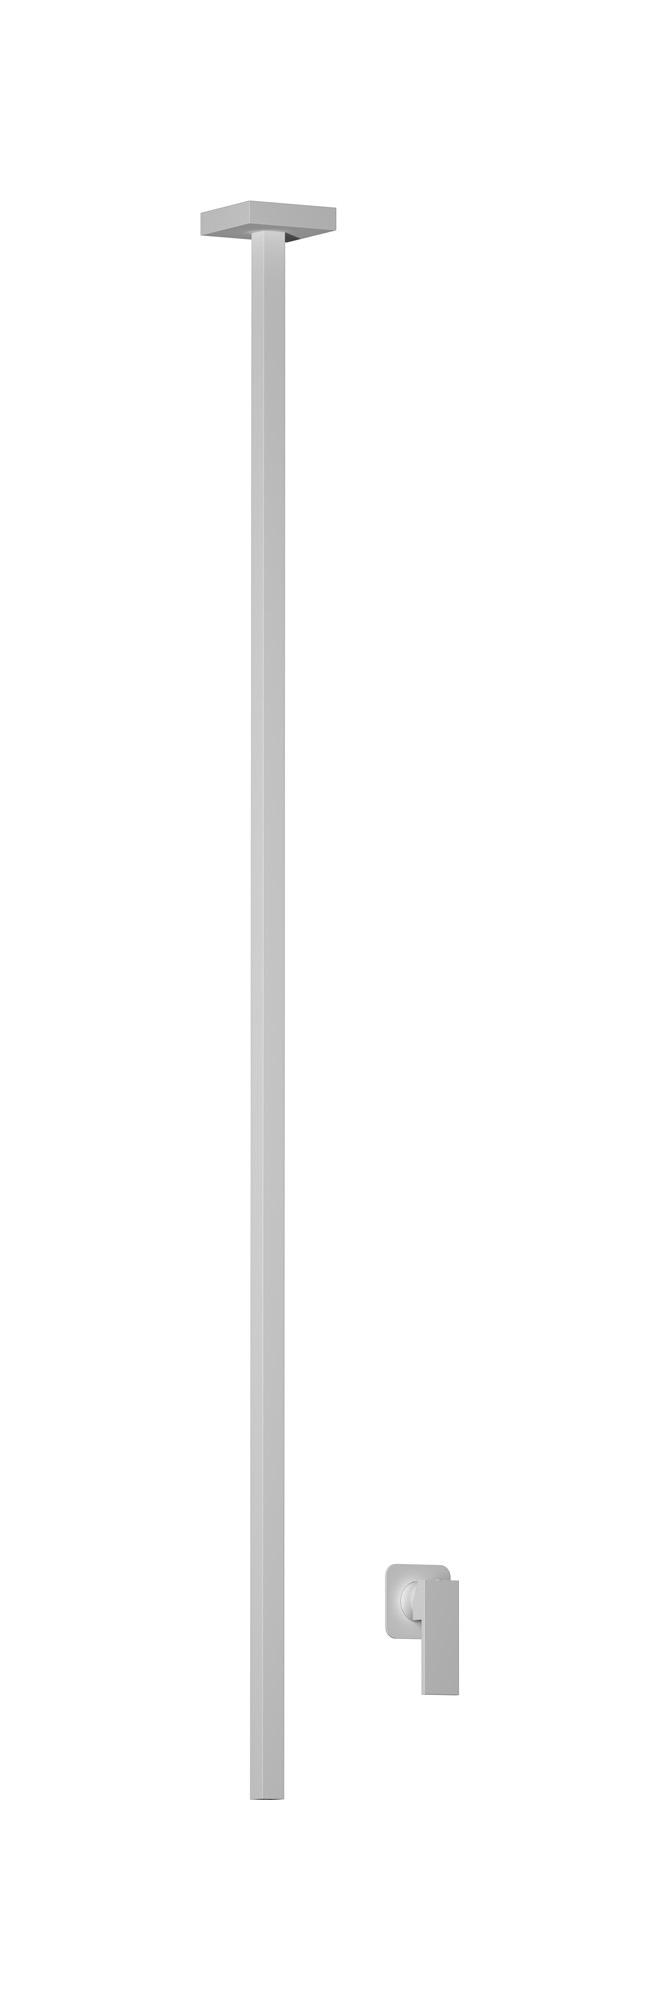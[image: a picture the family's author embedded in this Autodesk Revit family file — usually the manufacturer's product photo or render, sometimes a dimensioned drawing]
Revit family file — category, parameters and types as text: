
# Revit family: RU210
name_source: partatom
category: Apparecchi idraulici
units: mm (PartAtom-declared; Revit-internal decimal feet)

## family parameters
Basato su piano di lavoro = No
Condiviso = No
Mantieni orientamento annotazione = No
Numero OmniClass = 23.45.55.17
Punto di calcolo locali = No
Quota connettore circolare = Usa diametro
Sempre verticale = Sì
Taglio con vuoti quando caricato = No
Tipo di parte = Normale
Titolo OmniClass = Mixing Faucets

## types (4) — shared parameters
Cold water inlet = 10 mm  [stored 0.0328084 ft]
Commenti sul tipo = Ceiling spout with wall mounted mixer
Connessione CW = No
Connessione HW = No
Connessione di scarico = No
Connessione di ventilazione = No
Descrizione = Ceiling spout with wall mounted mixer
Hot water inlet = 10 mm  [stored 0.0328084 ft]
Produttore = IB Rubinetterie S.p.A.
URL = https://www.weareib.it
zero-valued in all types: Prospetto di default

## per-type parameters (varying)
| type | Finishes surface | Immagine tipo | Modello |
| Chrome | IB_Chrome | RU210CC.jpg | RU210CC |
| Matt White | IB_matt white | RU210BO.jpg | RU210BO |
| Matt Black | IB_matt black | RU210NP.jpg | RU210NP |
| Brushed Nickel | IB_Brushed nickel | RU210SS.jpg | RU210SS |

note: [stored X ft] marks values corroborated as IEEE doubles in the binary element streams (Revit-internal decimal feet)
